# Revit family: ADB Fourneaux Gaz  Géant L10002
name_source: partatom
category: Equipement spécialisé
units: mm (PartAtom-declared; Revit-internal decimal feet)

## family parameters
Basée sur le plan de construction = Non
Conserver l'orientation des annotations = Non
Cote de connecteur circulaire = Utiliser le diamètre
Couper avec des vides une fois chargée = Non
Numéro OmniClass = 23.40.40.14.17.11
Partagée = Non
Repère de localisation dans la pièce = Non
Titre OmniClass = Cookers, Ovens, Stoves
Toujours verticalement = Oui
Type d'élément = Normal

## types (2) — shared parameters
Commentaires du type = Gamme Ambassade - Fourneaux gaz
Description = Fourneau 5 feux vifs - 1 four gaz 137L
Diamètre de Raccordement Gaz = 21 mm
Fabricant = Société Industrielle de Lacanche
Modèle = CG 1051 B
Pbase = 0 W
Poids net à vide = 128.00 kg
URL = https://www.ambassade-de-bourgogne.com
zero-valued in all types: Elévation par défaut

## per-type parameters (varying)
| type | Pbase gaz |
| 5 feux vifs - 1 four - option SFEB001 _ CG 1051 B | 19 W |
| 5 feux vifs - 1 four - CG 1051 B | 26 W |
